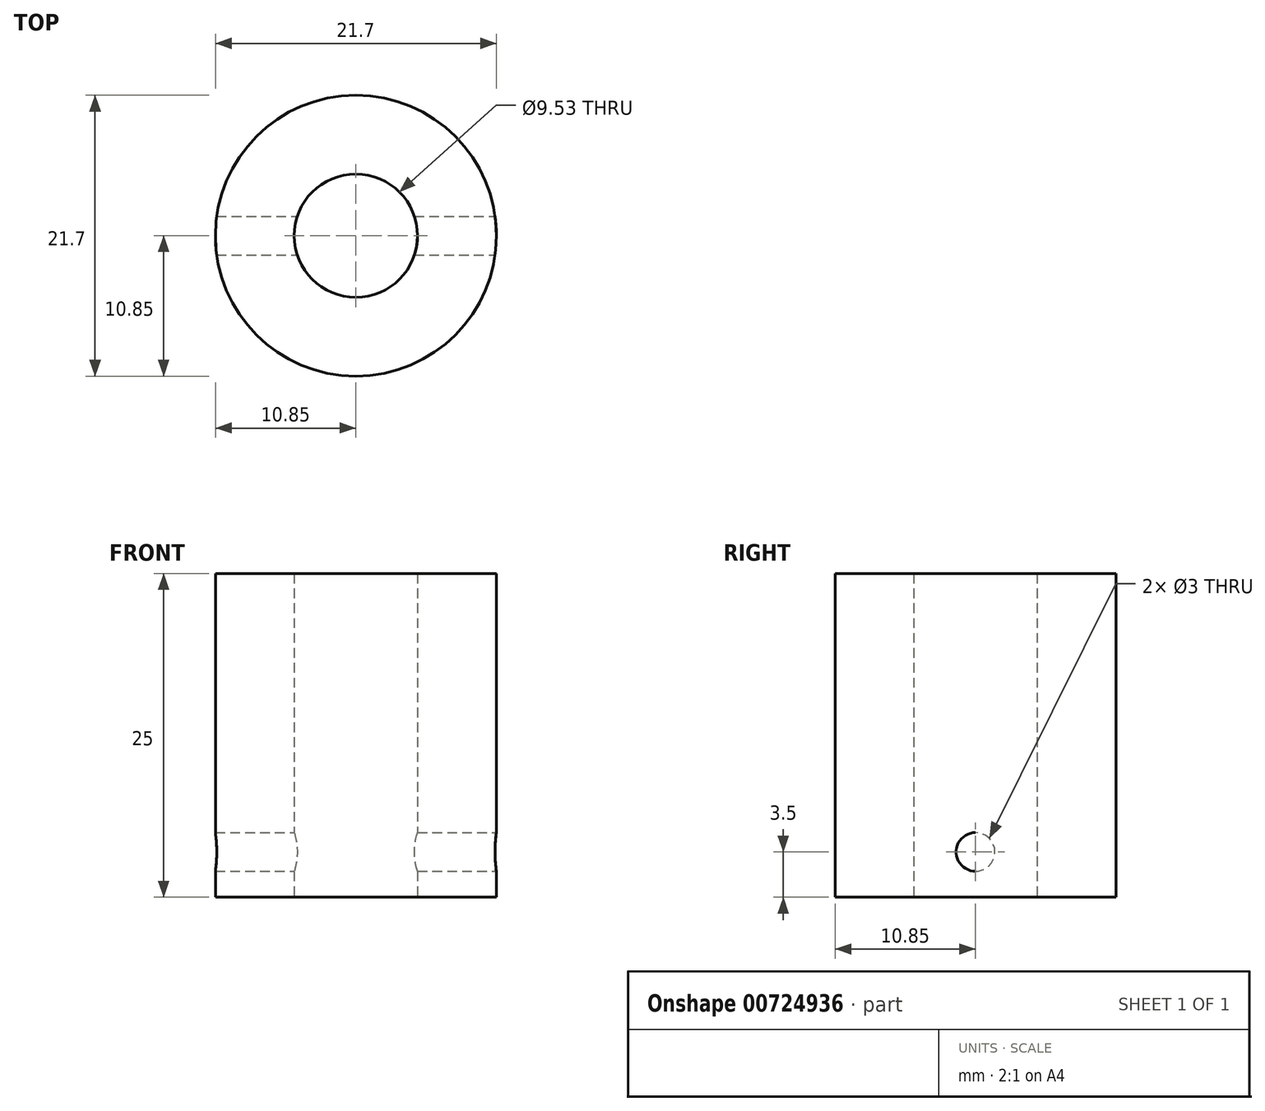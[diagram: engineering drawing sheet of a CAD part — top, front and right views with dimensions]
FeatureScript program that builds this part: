
annotation { "Feature Type Name" : "Feature", "Feature Type Description" : "" }
export const myFeature = defineFeature(function(context is Context, id is Id, definition is map)
    precondition{}
    {
        {
            var Q0;
            Q0=qCreatedBy(makeId("Top.planeOp"),FACE);
            var sketch = newSketch(context, id + "F0", { "sketchPlane" : qUnion([Q0])});
            skCircle(sketch, "E0", {"center": v(0, 0) * mm, "radius": 10.85 * mm});
            skCircle(sketch, "E1", {"center": v(0, 0) * mm, "radius": 4.76 * mm});
            skSolve(sketch);
        }
        {
            var Q0;
            Q0=makeQuery(id+"F0.imprint","IMPRINT",FACE,{"disambiguationData":[TD([[makeQuery(id+"F0.imprint","IMPRINT",EDGE,{"derivedFrom":sQuery(id+"F0.wireOp",EDGE,"E0")}),1.0]])]});
            extrude(context, id + "F1", {"entities" : qUnion([Q0]), "depth" : 25 * mm, "offsetDistance" : 25 * mm});
        }
        {
            var Q0;
            Q0=qCreatedBy(makeId("Right.planeOp"),FACE);
            var sketch = newSketch(context, id + "F2", { "sketchPlane" : qUnion([Q0])});
            skCircle(sketch, "E2", {"center": v(0, 3.5) * mm, "radius": 1.5 * mm});
            skSolve(sketch);
        }
        {
            var Q0;
            Q0 = qSketchRegion(id + "F2", true);
            extrude(context, id + "F3", {"entities" : qUnion([Q0]), "operationType" : NewBodyOperationType.REMOVE, "endBound" : BoundingType.SYMMETRIC, "oppositeDirection" : true, "depth" : 25 * mm, "offsetDistance" : 25 * mm});
        }
    });
